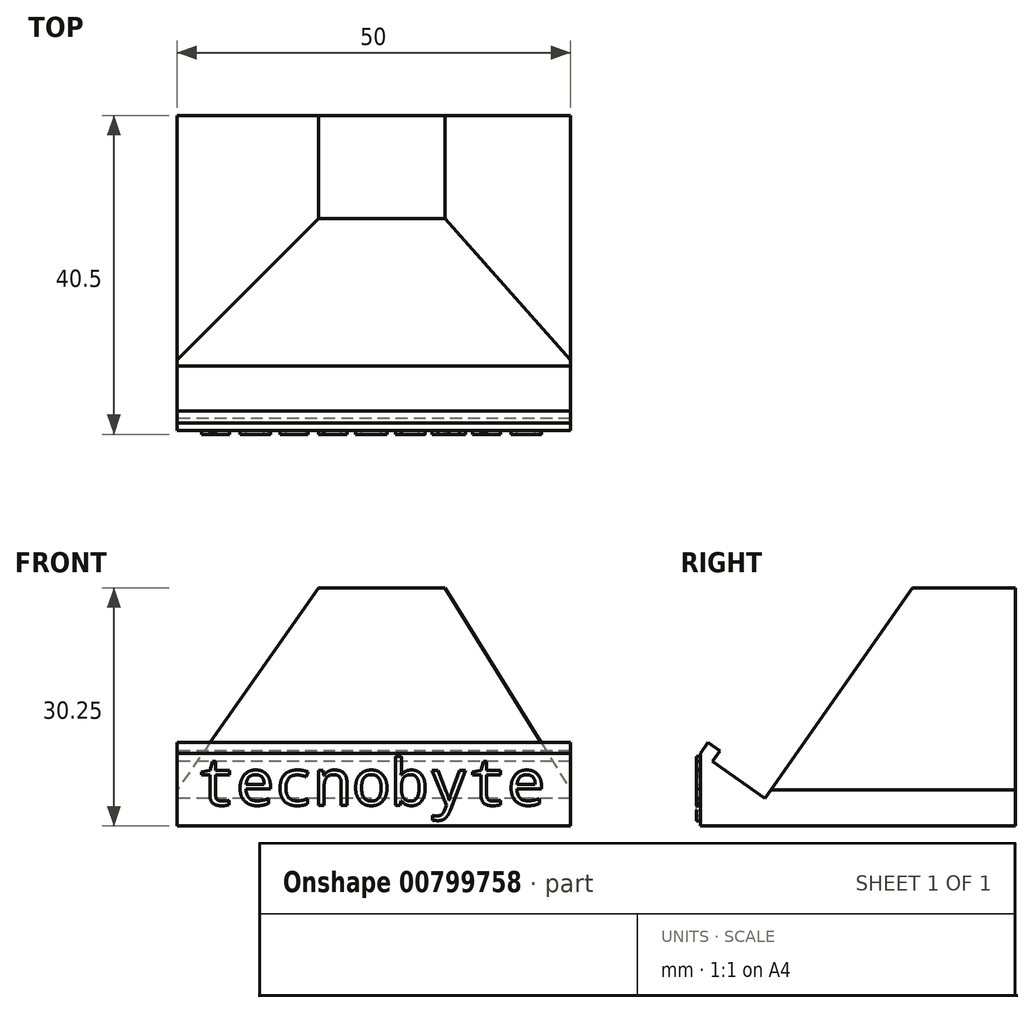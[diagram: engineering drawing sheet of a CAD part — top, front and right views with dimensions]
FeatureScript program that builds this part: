
annotation { "Feature Type Name" : "Feature", "Feature Type Description" : "" }
export const myFeature = defineFeature(function(context is Context, id is Id, definition is map)
    precondition{}
    {
        {
            var Q0;
            Q0=qCreatedBy(makeId("Right.planeOp"),FACE);
            var sketch = newSketch(context, id + "F0", { "sketchPlane" : qUnion([Q0])});
            skLineSegment(sketch, "E0", {"start": v(6.9, 0) * mm, "end": v(6.9, 9.24) * mm});
            skLineSegment(sketch, "E1", {"start": v(6.9, 0) * mm, "end": v(46.9, 0) * mm});
            skLineSegment(sketch, "E2", {"start": v(46.9, 0) * mm, "end": v(46.9, 30.25) * mm});
            skLineSegment(sketch, "E3", {"start": v(46.9, 30.25) * mm, "end": v(33.82, 30.25) * mm});
            skLineSegment(sketch, "E4", {"start": v(33.82, 30.25) * mm, "end": v(15.1, 3.5) * mm});
            skLineSegment(sketch, "E5", {"start": v(15.1, 3.5) * mm, "end": v(6.9, 9.24) * mm});
            skLineSegment(sketch, "E6", {"start": v(8.43, 8.17) * mm, "end": v(9.38, 9.53) * mm});
            skLineSegment(sketch, "E7", {"start": v(9.38, 9.53) * mm, "end": v(7.85, 10.6) * mm});
            skLineSegment(sketch, "E8", {"start": v(7.85, 10.6) * mm, "end": v(6.9, 9.24) * mm});
            skSolve(sketch);
        }
        {
            var Q0;
            {var subQ0=sQuery(id+"F0.wireOp",EDGE,"E0");Q0=makeQuery(id+"F0.imprint","IMPRINT",FACE,{"disambiguationData":[TD([[makeQuery(id+"F0.imprint","IMPRINT",EDGE,{"derivedFrom":subQ0}),-1.0]])]});}
            var Q1;
            {var subQ2=sQuery(id+"F0.wireOp",EDGE,"E6");Q1=makeQuery(id+"F0.imprint","IMPRINT",FACE,{"disambiguationData":[TD([[makeQuery(id+"F0.imprint","IMPRINT",EDGE,{"derivedFrom":subQ2}),1.0]])]});}
            extrude(context, id + "F1", {"entities" : qUnion([Q0, Q1]), "depth" : 50 * mm, "offsetDistance" : 25 * mm});
        }
        {
            var Q0;
            Q0=makeQuery(id+"F1.opExtrude","SWEPT_FACE",FACE,{"disambiguationData":[OSD([sQuery(id+"F0.wireOp",EDGE,"E2")])]});
            var sketch = newSketch(context, id + "F2", { "sketchPlane" : qUnion([Q0])});
            skLineSegment(sketch, "E9", {"start": v(-50, 4.57) * mm, "end": v(-34.07, 30.25) * mm});
            skLineSegment(sketch, "E10", {"start": v(-50, 4.57) * mm, "end": v(0, 4.57) * mm, "construction": true});
            skLineSegment(sketch, "E11", {"start": v(0, 4.57) * mm, "end": v(-18.02, 30.25) * mm});
            skSolve(sketch);
        }
        {
            var Q0;
            {var subQ0=sQuery(id+"F2.wireOp",EDGE,"E9");Q0=makeQuery(id+"F2.imprint","IMPRINT",FACE,{"disambiguationData":[TD([[makeQuery(id+"F2.imprint","IMPRINT",EDGE,{"derivedFrom":subQ0}),1.0]])]});}
            var Q1;
            {var subQ0=sQuery(id+"F2.wireOp",EDGE,"E11");Q1=makeQuery(id+"F2.imprint","IMPRINT",FACE,{"disambiguationData":[TD([[makeQuery(id+"F2.imprint","IMPRINT",EDGE,{"derivedFrom":subQ0}),-1.0]])]});}
            var Q2;
            Q2=makeQuery(id+"F1.opExtrude","SWEPT_FACE",FACE,{"disambiguationData":[OSD([sQuery(id+"F0.wireOp",EDGE,"E4")])]});
            extrude(context, id + "F3", {"entities" : qUnion([Q0, Q1]), "operationType" : NewBodyOperationType.REMOVE, "endBound" : BoundingType.UP_TO_SURFACE, "oppositeDirection" : true, "depth" : 25 * mm, "endBoundEntityFace" : qUnion([Q2]), "offsetDistance" : 25 * mm});
        }
        {
            var Q0;
            Q0=makeQuery(id+"F1.opExtrude","SWEPT_FACE",FACE,{"disambiguationData":[OSD([sQuery(id+"F0.wireOp",EDGE,"E0")])]});
            var sketch = newSketch(context, id + "F4", { "sketchPlane" : qUnion([Q0])});
            skText(sketch, "E12", { "text": "tecnobyte", "fontName": "DroidSansMono.ttf"});
            const initialGuessF4  = {"E12": [0.00257, 0.00264, 1, 0, 0.0059]};
            skSetInitialGuess(sketch, initialGuessF4);
            skSolve(sketch);
        }
        {
            var Q0;
            Q0 = qSketchRegion(id + "F4", true);
            extrude(context, id + "F5", {"entities" : qUnion([Q0]), "operationType" : NewBodyOperationType.ADD, "depth" : 0.5 * mm, "offsetDistance" : 25 * mm});
        }
    });
